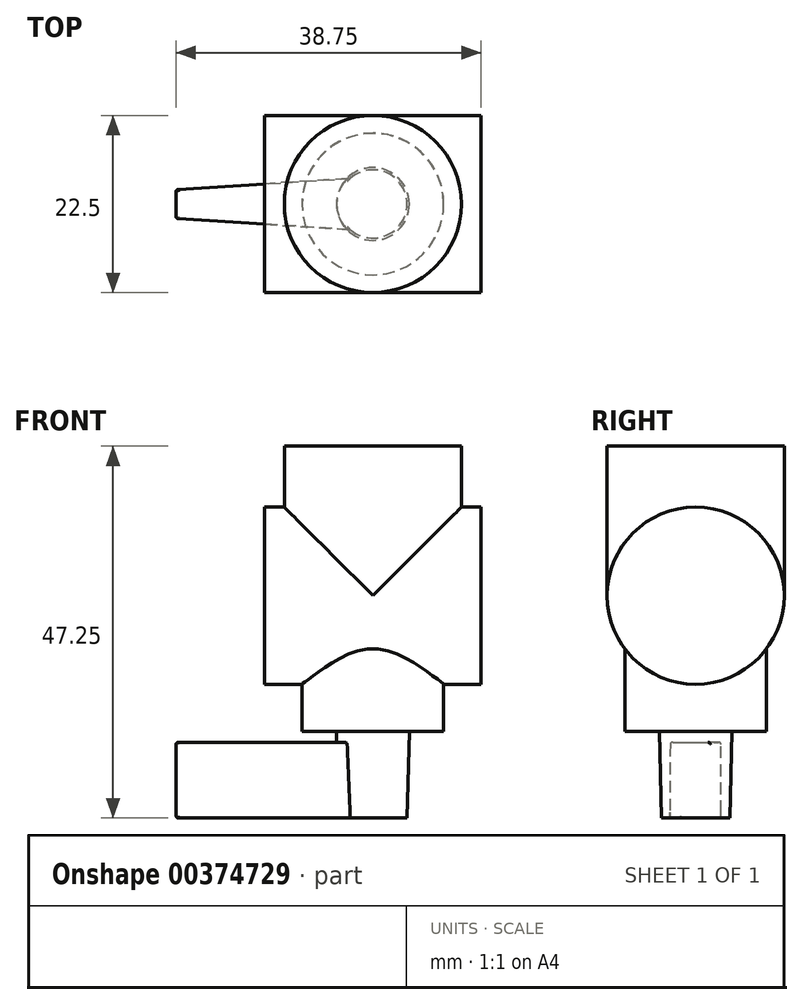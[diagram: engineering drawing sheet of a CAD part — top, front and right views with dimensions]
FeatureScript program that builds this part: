
annotation { "Feature Type Name" : "Feature", "Feature Type Description" : "" }
export const myFeature = defineFeature(function(context is Context, id is Id, definition is map)
    precondition{}
    {
        {
            var Q0;
            Q0=qCreatedBy(makeId("Top.planeOp"),FACE);
            var sketch = newSketch(context, id + "F0", { "sketchPlane" : qUnion([Q0])});
            skCircle(sketch, "E0", {"center": v(0, 0) * mm, "radius": 11.25 * mm});
            skSolve(sketch);
        }
        {
            var Q0;
            Q0 = qSketchRegion(id + "F0", true);
            extrude(context, id + "F1", {"entities" : qUnion([Q0]), "oppositeDirection" : true, "depth" : 19 * mm});
        }
        {
            var Q0;
            Q0=qCreatedBy(makeId("Right.planeOp"),FACE);
            var sketch = newSketch(context, id + "F2", { "sketchPlane" : qUnion([Q0])});
            skCircle(sketch, "E1", {"center": v(0, -19) * mm, "radius": 11.25 * mm});
            skSolve(sketch);
        }
        {
            var Q0;
            Q0 = qSketchRegion(id + "F2", true);
            extrude(context, id + "F3", {"entities" : qUnion([Q0]), "operationType" : NewBodyOperationType.ADD, "endBound" : BoundingType.SYMMETRIC, "depth" : 27.5 * mm});
        }
        {
            var Q0;
            Q0=qCreatedBy(makeId("Top.planeOp"),FACE);
            var sketch = newSketch(context, id + "F4", { "sketchPlane" : qUnion([Q0])});
            skCircle(sketch, "E2", {"center": v(0, 0) * mm, "radius": 9 * mm});
            skSolve(sketch);
        }
        {
            var Q0;
            Q0 = qSketchRegion(id + "F4", true);
            extrude(context, id + "F5", {"entities" : qUnion([Q0]), "operationType" : NewBodyOperationType.ADD, "oppositeDirection" : true, "depth" : 36.25 * mm});
        }
        {
            var Q0;
            Q0=makeQuery(id+"F5.opExtrude","CAP_FACE",FACE,{"disambiguationData":[OSD([sQuery(id+"F4.wireOp",EDGE,"E2")])],"isStart":false});
            var sketch = newSketch(context, id + "F6", { "sketchPlane" : qUnion([Q0])});
            skCircle(sketch, "E3", {"center": v(0, 0) * mm, "radius": 4.62 * mm});
            skSolve(sketch);
        }
        {
            var Q0;
            Q0 = qSketchRegion(id + "F6", true);
            extrude(context, id + "F7", {"entities" : qUnion([Q0]), "operationType" : NewBodyOperationType.ADD, "depth" : 11 * mm, "hasDraft" : true, "draftAngle" : 1.5 * degree, "draftPullDirection" : true});
        }
        {
            var Q0;
            Q0=qCreatedBy(makeId("Right.planeOp"),FACE);
            var sketch = newSketch(context, id + "F8", { "sketchPlane" : qUnion([Q0])});
            skLineSegment(sketch, "E4", {"start": v(0, -47.28) * mm, "end": v(0, -37.58) * mm, "construction": true});
            skLineSegment(sketch, "E5.bottom", {"start": v(-3.25, -47.25) * mm, "end": v(3.25, -47.25) * mm});
            skLineSegment(sketch, "E5.top", {"start": v(-3.25, -37.61) * mm, "end": v(3.25, -37.61) * mm});
            skLineSegment(sketch, "E5.left", {"start": v(-3.25, -47.25) * mm, "end": v(-3.25, -37.61) * mm});
            skLineSegment(sketch, "E5.right", {"start": v(3.25, -47.25) * mm, "end": v(3.25, -37.61) * mm});
            skPoint(sketch, "E5.middle", {"position": v(0, -42.43) * mm});
            skSolve(sketch);
        }
        {
            var Q0;
            Q0 = qSketchRegion(id + "F8", true);
            extrude(context, id + "F9", {"entities" : qUnion([Q0]), "operationType" : NewBodyOperationType.ADD, "oppositeDirection" : true, "depth" : 25 * mm});
        }
        {
            var Q0;
            Q0=makeQuery(id+"F9.opExtrude","CAP_EDGE",EDGE,{"disambiguationData":[OSD([sQuery(id+"F8.wireOp",EDGE,"E5.right")])],"isStart":false});
            var Q1;
            Q1=makeQuery(id+"F9.opExtrude","CAP_EDGE",EDGE,{"disambiguationData":[OSD([sQuery(id+"F8.wireOp",EDGE,"E5.left")])],"isStart":false});
            chamfer(context, id + "F10", {"entities" : qUnion([Q0, Q1]), "chamferType" : ChamferType.TWO_OFFSETS, "width1" : 22.1 * mm, "oppositeDirection" : false, "width2" : 1.4 * mm, "tangentPropagation" : true});
        }
        {
            var Q0;
            {var subQ0=sQuery(id+"F8.wireOp",EDGE,"E5.right");Q0=makeQuery(id+"F10.opChamfer","BLEND_EDGE",EDGE,{"blendedFrom":[makeQuery(id+"F9.opExtrude","CAP_EDGE",EDGE,{"disambiguationData":[OSD([subQ0])],"isStart":false}),makeQuery(id+"F9.opExtrude","CAP_FACE",FACE,{"disambiguationData":[OSD([sQuery(id+"F8.wireOp",EDGE,"E5.bottom"),sQuery(id+"F8.wireOp",EDGE,"E5.top"),sQuery(id+"F8.wireOp",EDGE,"E5.left"),subQ0])],"isStart":false})],"blendedInto":[makeQuery(id+"F9.opExtrude","CAP_FACE",FACE,{"disambiguationData":[OSD([sQuery(id+"F8.wireOp",EDGE,"E5.bottom"),sQuery(id+"F8.wireOp",EDGE,"E5.top"),sQuery(id+"F8.wireOp",EDGE,"E5.left"),subQ0])],"isStart":false})]});}
            var Q1;
            {var subQ0=sQuery(id+"F8.wireOp",EDGE,"E5.left");Q1=makeQuery(id+"F10.opChamfer","BLEND_EDGE",EDGE,{"blendedFrom":[makeQuery(id+"F9.opExtrude","CAP_EDGE",EDGE,{"disambiguationData":[OSD([subQ0])],"isStart":false}),makeQuery(id+"F9.opExtrude","CAP_FACE",FACE,{"disambiguationData":[OSD([sQuery(id+"F8.wireOp",EDGE,"E5.bottom"),sQuery(id+"F8.wireOp",EDGE,"E5.top"),subQ0,sQuery(id+"F8.wireOp",EDGE,"E5.right")])],"isStart":false})],"blendedInto":[makeQuery(id+"F9.opExtrude","CAP_FACE",FACE,{"disambiguationData":[OSD([sQuery(id+"F8.wireOp",EDGE,"E5.bottom"),sQuery(id+"F8.wireOp",EDGE,"E5.top"),subQ0,sQuery(id+"F8.wireOp",EDGE,"E5.right")])],"isStart":false})]});}
            var Q2;
            Q2=makeQuery(id+"F9.opExtrude","CAP_EDGE",EDGE,{"disambiguationData":[OSD([sQuery(id+"F8.wireOp",EDGE,"E5.bottom")])],"isStart":false});
            var Q3;
            Q3=makeQuery(id+"F10.opChamfer","BLEND_EDGE",EDGE,{"blendedFrom":[makeQuery(id+"F9.opExtrude","CAP_EDGE",EDGE,{"disambiguationData":[OSD([sQuery(id+"F8.wireOp",EDGE,"E5.right")])],"isStart":false}),makeQuery(id+"F9.opExtrude","SWEPT_FACE",FACE,{"disambiguationData":[OSD([sQuery(id+"F8.wireOp",EDGE,"E5.bottom")])]})],"blendedInto":[makeQuery(id+"F9.opExtrude","SWEPT_FACE",FACE,{"disambiguationData":[OSD([sQuery(id+"F8.wireOp",EDGE,"E5.bottom")])]})]});
            var Q4;
            Q4=makeQuery(id+"F10.opChamfer","BLEND_EDGE",EDGE,{"blendedFrom":[makeQuery(id+"F9.opExtrude","CAP_EDGE",EDGE,{"disambiguationData":[OSD([sQuery(id+"F8.wireOp",EDGE,"E5.left")])],"isStart":false}),makeQuery(id+"F9.opExtrude","SWEPT_FACE",FACE,{"disambiguationData":[OSD([sQuery(id+"F8.wireOp",EDGE,"E5.bottom")])]})],"blendedInto":[makeQuery(id+"F9.opExtrude","SWEPT_FACE",FACE,{"disambiguationData":[OSD([sQuery(id+"F8.wireOp",EDGE,"E5.bottom")])]})]});
            var Q5;
            Q5=makeQuery(id+"F10.opChamfer","BLEND_EDGE",EDGE,{"blendedFrom":[makeQuery(id+"F9.opExtrude","CAP_EDGE",EDGE,{"disambiguationData":[OSD([sQuery(id+"F8.wireOp",EDGE,"E5.right")])],"isStart":false}),makeQuery(id+"F9.opExtrude","SWEPT_FACE",FACE,{"disambiguationData":[OSD([sQuery(id+"F8.wireOp",EDGE,"E5.top")])]})],"blendedInto":[makeQuery(id+"F9.opExtrude","SWEPT_FACE",FACE,{"disambiguationData":[OSD([sQuery(id+"F8.wireOp",EDGE,"E5.top")])]})]});
            var Q6;
            Q6=makeQuery(id+"F9.opExtrude","CAP_EDGE",EDGE,{"disambiguationData":[OSD([sQuery(id+"F8.wireOp",EDGE,"E5.top")])],"isStart":false});
            var Q7;
            Q7=makeQuery(id+"F10.opChamfer","BLEND_EDGE",EDGE,{"blendedFrom":[makeQuery(id+"F9.opExtrude","CAP_EDGE",EDGE,{"disambiguationData":[OSD([sQuery(id+"F8.wireOp",EDGE,"E5.left")])],"isStart":false}),makeQuery(id+"F9.opExtrude","SWEPT_FACE",FACE,{"disambiguationData":[OSD([sQuery(id+"F8.wireOp",EDGE,"E5.top")])]})],"blendedInto":[makeQuery(id+"F9.opExtrude","SWEPT_FACE",FACE,{"disambiguationData":[OSD([sQuery(id+"F8.wireOp",EDGE,"E5.top")])]})]});
            fillet(context, id + "F11", {"entities" : qUnion([Q0, Q1, Q2, Q3, Q4, Q5, Q6, Q7]), "radius" : .3 * mm, "tangentPropagation" : true, "allowEdgeOverflow" : false});
        }
    });
